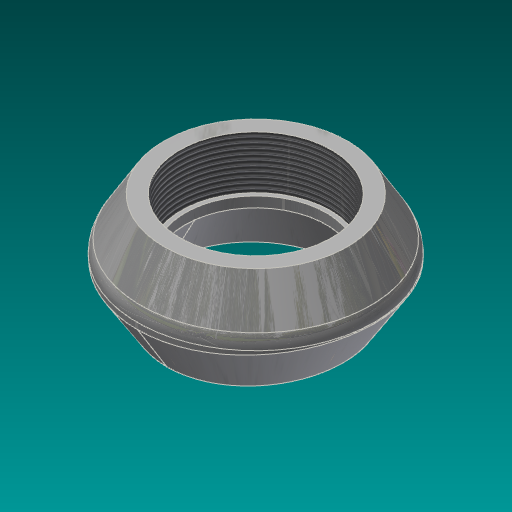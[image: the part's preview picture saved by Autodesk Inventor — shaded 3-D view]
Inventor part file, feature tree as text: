
AUTODESK INVENTOR PART (.ipt)
format: ipt  version: 2017.3 (Build 213256000, 256)  size: 449,024 bytes
history: native  units: mm (DEFAULTED — no unit token found)
features: other x8, sketch x5, plane x1, extrude x1, revolve x1, thread x1, sweep x1
ambient origin geometry x8: Origin, YZ Plane, XZ Plane, XY Plane, X Axis, Y Axis, Z Axis, Center Point
bodies: Solid1 (feature_tree)
feature tree (18):
  sketch  "Sketch1"  dims[d5=38.1mm d8=90.0deg]
  plane  "Work Plane1"
  sketch  "Sketch2"  dims[d9=0.0mm d10=949.325mm d11=10.0mm d12=0.0mm]
  extrude  "Extrusion1"  TaperAngle=90.0deg  [1 undecoded]
  revolve  "Revolution2"  [1 undecoded]
  thread  "Thread1"  [1 undecoded]
  other  "Work Point1"
  sweep  "Sweep1"
  other  "Work Axis3"
  other  "Work Point2"
  other  "Work Point3"
  sketch  "Sketch3"  dims[d45=8.810625mm d52=88.10625mm]
  sketch  "Sketch4"  dims[d54=1224.75625mm d77=68.1482mm d80=38.1mm d81=19.2151mm d83=56.55818mm d85=0.312398mm d86=90.0deg d91=52.5018mm d92=6.0mm d93=4.0mm d94=2.0mm d95=90.0deg d96=3.84302mm d97=0.0mm d102=10.0mm d103=0.0mm d106=19.05mm d107=512.7625mm d120=-474.6625mm d121=0.0mm d129=0.78232mm d130=0.78232mm d131=30.0deg d132=11.509375mm d133=0.0mm d134=0.0mm d135=90.0deg d136=0.0mm d137=90.0deg d138=65.0875mm d139=58.3692mm d140=0.0mm]
  other  "Work Axis2"
  sketch  "3D Sketch1"
  other  "Edges14"
  other  "Edges15"
  other  "Work Axis4"
note: 3 required parameter values undecoded (feature->parameter linkage not recoverable at this tier; creation-order binding heuristic only, values carry confidence <= 0.55)